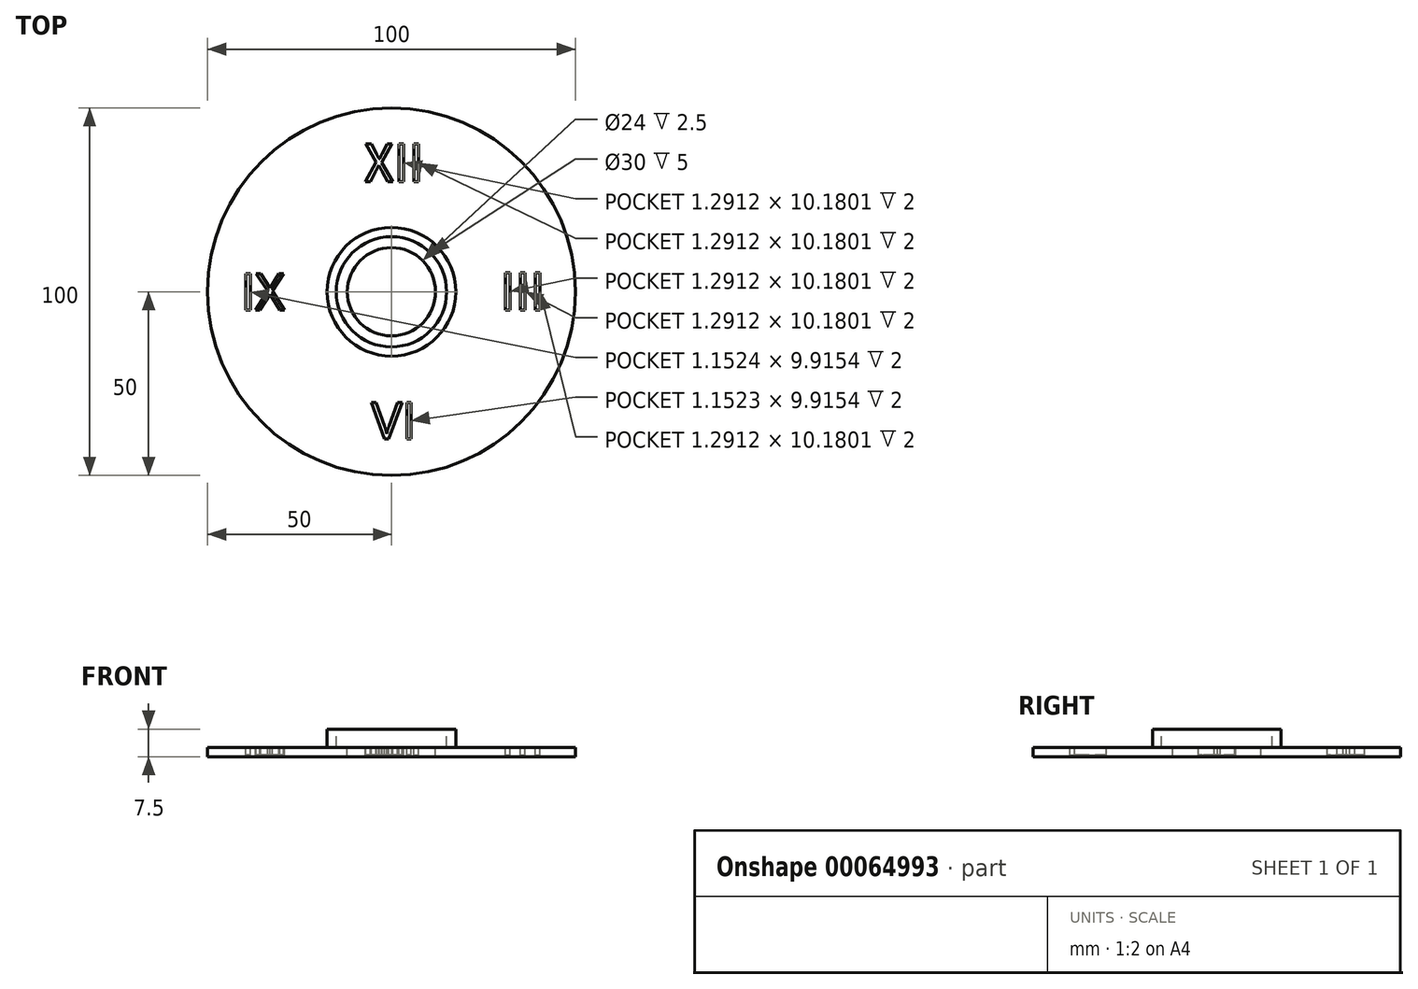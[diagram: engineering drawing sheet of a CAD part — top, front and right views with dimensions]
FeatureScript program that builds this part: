
annotation { "Feature Type Name" : "Feature", "Feature Type Description" : "" }
export const myFeature = defineFeature(function(context is Context, id is Id, definition is map)
    precondition{}
    {
        {
            var Q0;
            Q0=qCreatedBy(makeId("Front.planeOp"),FACE);
            var sketch = newSketch(context, id + "F0", { "sketchPlane" : qUnion([Q0])});
            skLineSegment(sketch, "E0.top", {"start": v(-15, 2.5) * mm, "end": v(0, 2.5) * mm});
            skLineSegment(sketch, "E0.left", {"start": v(-15, 7.5) * mm, "end": v(-15, 2.5) * mm});
            skLineSegment(sketch, "E1.0", {"start": v(-17.5, 0) * mm, "end": v(0, 0) * mm});
            skLineSegment(sketch, "E1.1", {"start": v(-17.5, 7.5) * mm, "end": v(-17.5, 2.5) * mm});
            skLineSegment(sketch, "E2", {"start": v(-15, 7.5) * mm, "end": v(-17.5, 7.5) * mm});
            skLineSegment(sketch, "E3.bottom", {"start": v(-17.5, 0) * mm, "end": v(-50, 0) * mm});
            skLineSegment(sketch, "E3.top", {"start": v(-17.5, 2.5) * mm, "end": v(-50, 2.5) * mm});
            skLineSegment(sketch, "E3.right", {"start": v(-50, 0) * mm, "end": v(-50, 2.5) * mm});
            skLineSegment(sketch, "E4", {"start": v(0, 2.5) * mm, "end": v(0, 0) * mm});
            skLineSegment(sketch, "E5", {"start": v(-12, 2.5) * mm, "end": v(-12, 0) * mm});
            skSolve(sketch);
        }
        {
            var Q0;
            {var subQ3=sQuery(id+"F0.wireOp",EDGE,"E0.left");Q0=makeQuery(id+"F0.imprint","IMPRINT",FACE,{"disambiguationData":[TD([[makeQuery(id+"F0.imprint","IMPRINT",EDGE,{"derivedFrom":subQ3}),-1.0]])]});}
            var Q1;
            Q1=sQuery(id+"F0.wireOp",EDGE,"E4");
            revolve(context, id + "F1", {"entities" : qUnion([Q0]), "axis" : qUnion([Q1]), "revolveType" : RevolveType.FULL});
        }
        {
            var Q0;
            Q0=makeQuery(id+"F1.opRevolve","SWEPT_FACE",FACE,{"disambiguationData":[OSD([sQuery(id+"F0.wireOp",EDGE,"E3.top")])]});
            var sketch = newSketch(context, id + "F2", { "sketchPlane" : qUnion([Q0])});
            skCircle(sketch, "E6", {"center": v(0, 0) * mm, "radius": 35 * mm, "construction": true});
            skText(sketch, "E7", { "text": "XII", "fontName": "NotoSansCJKtc-Regular.otf"});
            skPoint(sketch, "E8", {"position": v(0, 35) * mm});
            skPoint(sketch, "E9", {"position": v(0, -35) * mm});
            skPoint(sketch, "E10", {"position": v(35, 0) * mm});
            skPoint(sketch, "E11", {"position": v(-35, 0) * mm});
            skText(sketch, "E12", { "text": "III", "fontName": "NotoSansCJKtc-Regular.otf"});
            skText(sketch, "E13", { "text": "VI", "fontName": "OpenSans-Regular.ttf"});
            skText(sketch, "E14", { "text": "IX", "fontName": "OpenSans-Regular.ttf"});
            const initialGuessF2  = {"E7": [-0.00735, 0.03, 1, 0, 0.01], "E12": [0.0296, -0.005, 1, 0, 0.01], "E13": [-0.0054, -0.04, 1, 0, 0.01], "E14": [-0.04092, -0.005, 1, 0, 0.01]};
            skSetInitialGuess(sketch, initialGuessF2);
            skSolve(sketch);
        }
        {
            var Q0;
            Q0 = qSketchRegion(id + "F2", true);
            extrude(context, id + "F3", {"entities" : qUnion([Q0]), "operationType" : NewBodyOperationType.REMOVE, "oppositeDirection" : true, "depth" : 2 * mm});
        }
    });
